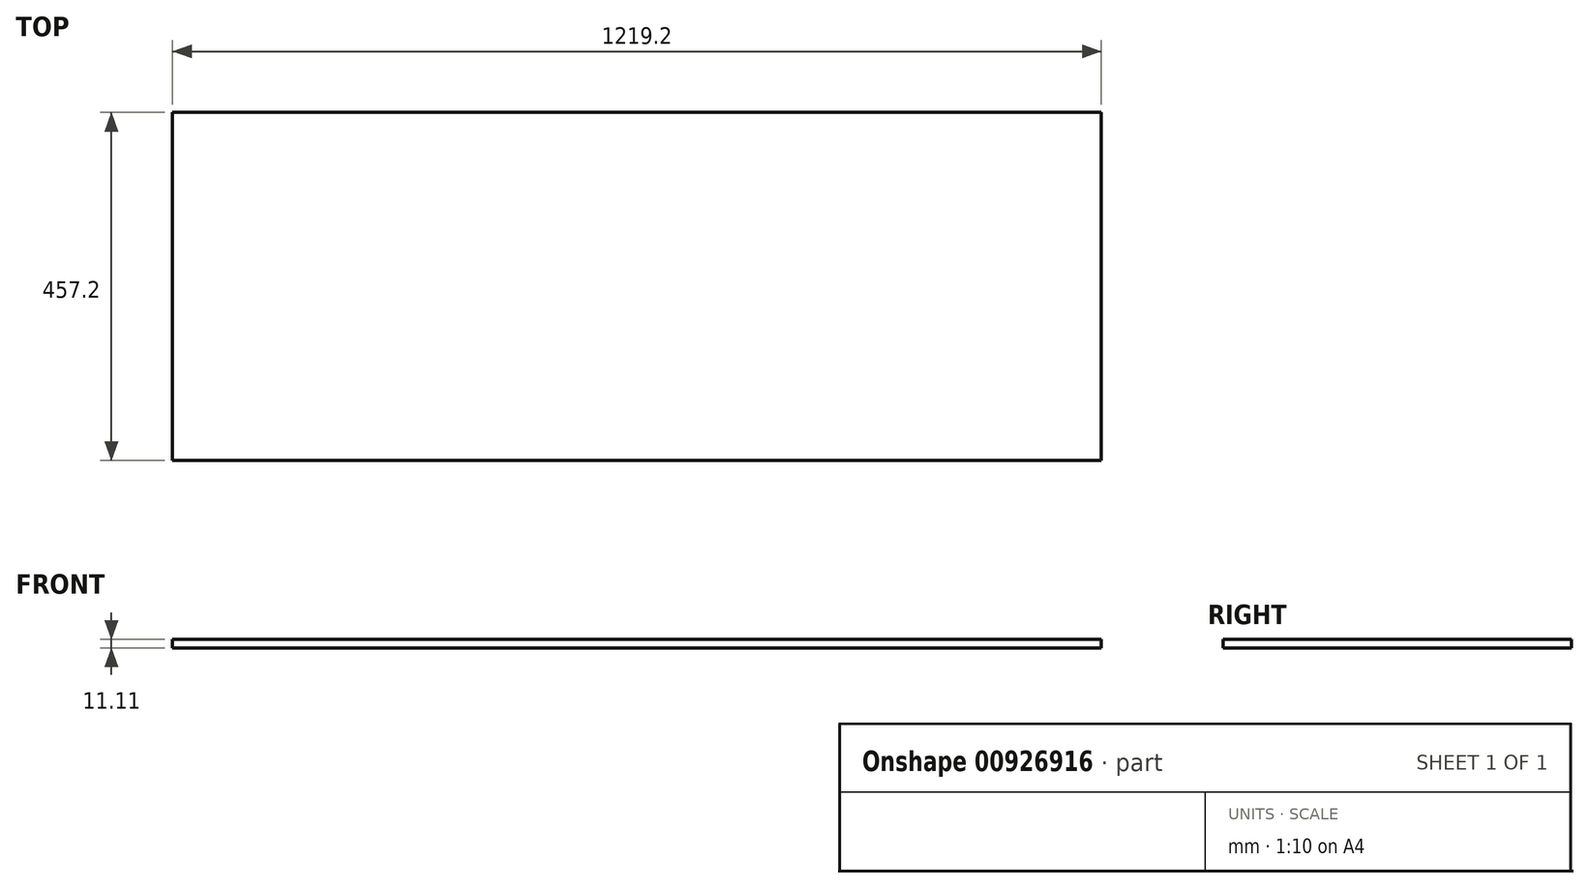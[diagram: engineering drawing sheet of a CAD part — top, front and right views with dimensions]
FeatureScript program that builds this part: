
annotation { "Feature Type Name" : "Feature", "Feature Type Description" : "" }
export const myFeature = defineFeature(function(context is Context, id is Id, definition is map)
    precondition{}
    {
        {
            var Q0;
            Q0=qCreatedBy(makeId("Top.planeOp"),FACE);
            var sketch = newSketch(context, id + "F0", { "sketchPlane" : qUnion([Q0])});
            skLineSegment(sketch, "E0.bottom", {"start": v(-547.07, 225.99) * mm, "end": v(672.13, 225.99) * mm});
            skLineSegment(sketch, "E0.top", {"start": v(-547.07, -231.21) * mm, "end": v(672.13, -231.21) * mm});
            skLineSegment(sketch, "E0.left", {"start": v(-547.07, 225.99) * mm, "end": v(-547.07, -231.21) * mm});
            skLineSegment(sketch, "E0.right", {"start": v(672.13, 225.99) * mm, "end": v(672.13, -231.21) * mm});
            skSolve(sketch);
        }
        {
            var Q0;
            Q0=makeQuery(id+"F0.imprint","IMPRINT",FACE,{"disambiguationData":[TD([[makeQuery(id+"F0.imprint","IMPRINT",EDGE,{"derivedFrom":sQuery(id+"F0.wireOp",EDGE,"E0.bottom")}),-1.0]])]});
            extrude(context, id + "F1", {"entities" : qUnion([Q0]), "depth" : 11.1 * mm, "offsetDistance" : 25.4 * mm});
        }
    });
